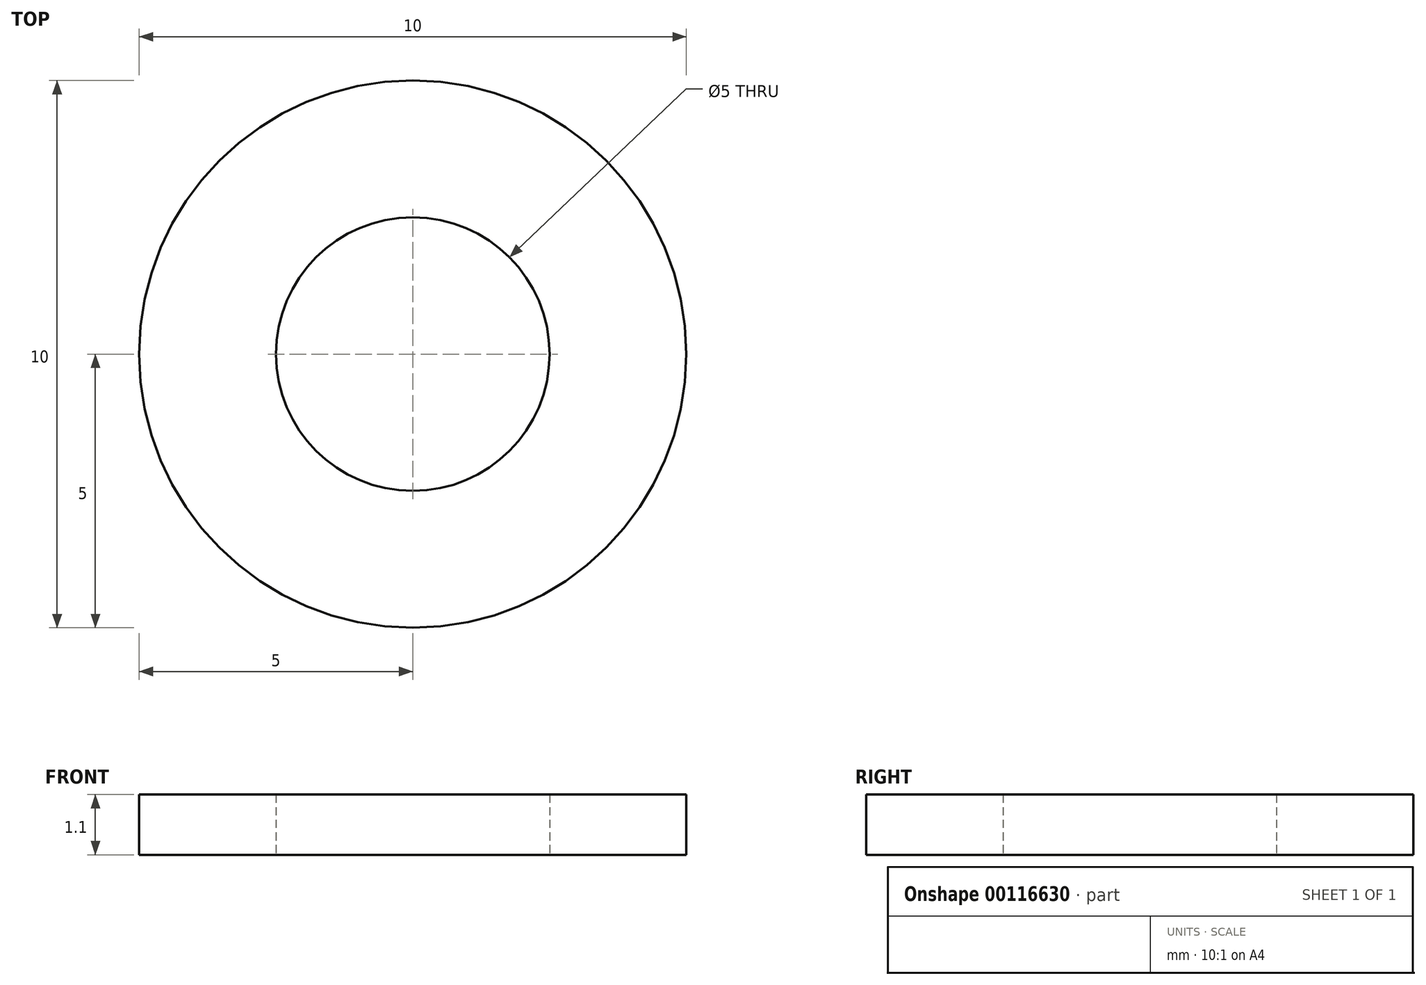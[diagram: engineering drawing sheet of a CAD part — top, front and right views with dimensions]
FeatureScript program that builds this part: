
annotation { "Feature Type Name" : "Feature", "Feature Type Description" : "" }
export const myFeature = defineFeature(function(context is Context, id is Id, definition is map)
    precondition{}
    {
        {
            var Q0;
            Q0=qCreatedBy(makeId("Top.planeOp"),FACE);
            var sketch = newSketch(context, id + "F0", { "sketchPlane" : qUnion([Q0])});
            skCircle(sketch, "E0", {"center": v(0, 0) * mm, "radius": 2.5 * mm});
            skCircle(sketch, "E1", {"center": v(0, 0) * mm, "radius": 5 * mm});
            skSolve(sketch);
        }
        {
            var Q0;
            Q0 = qSketchRegion(id + "F0", true);
            var Q1;
            Q1=makeQuery(id+"F0.imprint","IMPRINT",FACE,{"disambiguationData":[TD([[makeQuery(id+"F0.imprint","IMPRINT",EDGE,{"derivedFrom":sQuery(id+"F0.wireOp",EDGE,"E0")}),-1.0]])]});
            extrude(context, id + "F1", {"entities" : qUnion([Q0, Q1]), "depth" : 1.1 * mm});
        }
    });
